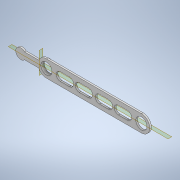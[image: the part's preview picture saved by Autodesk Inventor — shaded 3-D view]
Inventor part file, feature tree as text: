
AUTODESK INVENTOR PART (.ipt)
format: ipt  version: 2022 (Build 260153000, 153)  size: 206,848 bytes
history: native  units: mm
features: sketch x3, extrude x3, plane x2, pattern_circular x1, other x1
ambient origin geometry x8: Origin, YZ Plane, XZ Plane, XY Plane, X Axis, Y Axis, Z Axis, Center Point
bodies: Body1 (feature_tree)
feature tree (10):
  sketch  "Sketch2"  dims[d27=170.0mm d28=30.0mm]
  extrude  "Extrusion2"  Depth=30.0mm
  extrude  "Extrusion3"  Depth=20.0mm
  plane  "Work Plane1"
  sketch  "Sketch4"  dims[d29=20.0mm d30=20.0mm]
  plane  "Work Plane2"
  extrude  "Extrusion5"  Depth=10.0mm
  pattern_circular  "Circular Pattern1"  Count=2  [1 undecoded]
  other  "Work Axis3"
  sketch  "Sketch5"  dims[d31=16.0mm d32=15.0mm d41=20.0mm d43=34.0mm d44=10.0mm d46=10.0mm d48=41.0mm d49=3.0mm d50=0.0mm d51=25.0mm d52=3.0mm d53=0.0mm d57=2.0mm d62=90.0deg d63=0.5mm d64=2.0mm d65=0.0mm d66=30.0mm d67=360.0deg]
note: 1 required parameter value undecoded (feature->parameter linkage not recoverable at this tier; creation-order binding heuristic only, values carry confidence <= 0.55)
